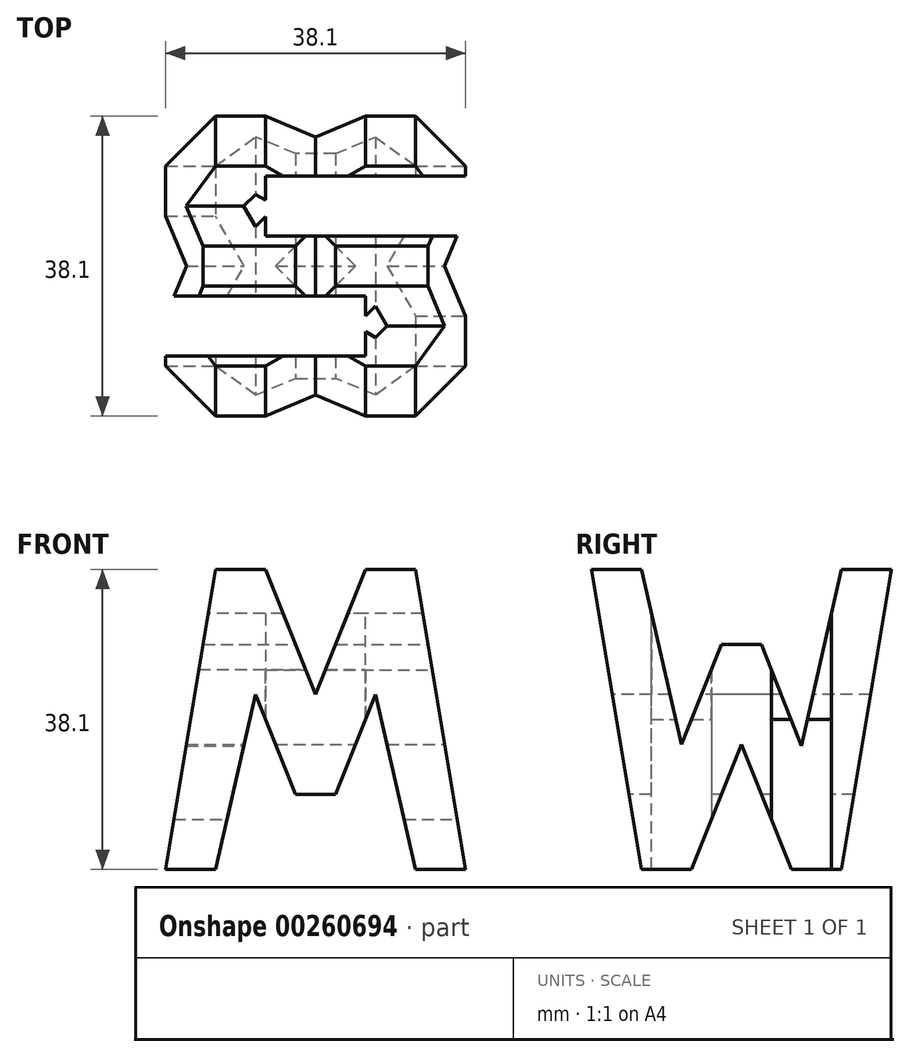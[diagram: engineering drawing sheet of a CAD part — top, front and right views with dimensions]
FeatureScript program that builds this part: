
annotation { "Feature Type Name" : "Feature", "Feature Type Description" : "" }
export const myFeature = defineFeature(function(context is Context, id is Id, definition is map)
    precondition{}
    {
        {
            var Q0;
            Q0=qCreatedBy(makeId("Front.planeOp"),FACE);
            var sketch = newSketch(context, id + "F0", { "sketchPlane" : qUnion([Q0])});
            skLineSegment(sketch, "E0", {"start": v(0, 0) * mm, "end": v(0, 38.1) * mm});
            skLineSegment(sketch, "E1", {"start": v(0, 0) * mm, "end": v(38.1, 0) * mm});
            skLineSegment(sketch, "E2", {"start": v(38.1, 0) * mm, "end": v(38.1, 38.1) * mm});
            skLineSegment(sketch, "E3", {"start": v(38.1, 38.1) * mm, "end": v(0, 38.1) * mm});
            skSolve(sketch);
        }
        {
            var Q0;
            Q0 = qSketchRegion(id + "F0", true);
            extrude(context, id + "F1", {"entities" : qUnion([Q0]), "depth" : 38.1 * mm});
        }
        {
            var Q0;
            Q0=qCreatedBy(makeId("Front.planeOp"),FACE);
            cPlane(context, id + "F2", {"entities" : qUnion([Q0]), "cplaneType" : CPlaneType.OFFSET, "offset" : 38.1 * mm, "width" : 152.4 * mm, "height" : 152.4 * mm});
        }
        {
            var Q0;
            Q0=qCreatedBy(makeId("Right.planeOp"),FACE);
            cPlane(context, id + "F3", {"entities" : qUnion([Q0]), "cplaneType" : CPlaneType.OFFSET, "offset" : 38.1 * mm, "width" : 152.4 * mm, "height" : 152.4 * mm});
        }
        {
            var Q0;
            Q0=qCreatedBy(makeId("Top.planeOp"),FACE);
            cPlane(context, id + "F4", {"entities" : qUnion([Q0]), "cplaneType" : CPlaneType.OFFSET, "offset" : 38.1 * mm, "width" : 152.4 * mm, "height" : 152.4 * mm});
        }
        {
            var Q0;
            Q0=qCreatedBy(id+"F3.planeOp",FACE);
            var sketch = newSketch(context, id + "F5", { "sketchPlane" : qUnion([Q0])});
            skLineSegment(sketch, "E4", {"start": v(0, 0) * mm, "end": v(0, 38.1) * mm});
            skLineSegment(sketch, "E5", {"start": v(0, 38.1) * mm, "end": v(-38.1, 38.1) * mm});
            skLineSegment(sketch, "E6", {"start": v(-38.1, 38.1) * mm, "end": v(-38.1, 0) * mm});
            skPoint(sketch, "E7.start.orphan", {"position": v(-19.05, 15.87) * mm});
            skPoint(sketch, "E8.start.orphan", {"position": v(-12.7, 0) * mm});
            skLineSegment(sketch, "E9", {"start": v(-6.35, 38.1) * mm, "end": v(-11.43, 15.67) * mm});
            skLineSegment(sketch, "E10", {"start": v(-11.43, 15.67) * mm, "end": v(-16.5, 28.57) * mm});
            skLineSegment(sketch, "E11", {"start": v(-16.5, 28.57) * mm, "end": v(-21.59, 28.57) * mm});
            skLineSegment(sketch, "E12", {"start": v(-21.59, 28.57) * mm, "end": v(-26.67, 15.87) * mm});
            skLineSegment(sketch, "E13", {"start": v(-26.67, 15.87) * mm, "end": v(-31.75, 38.1) * mm});
            skPoint(sketch, "E14.start.orphan", {"position": v(-31.75, 0) * mm});
            skPoint(sketch, "E15.start.orphan", {"position": v(-6.35, 0) * mm});
            skLineSegment(sketch, "E16", {"start": v(0, 38.1) * mm, "end": v(-6.35, 0) * mm});
            skLineSegment(sketch, "E17", {"start": v(-19.05, 15.87) * mm, "end": v(-25.4, 0) * mm});
            skLineSegment(sketch, "E18", {"start": v(-25.4, 0) * mm, "end": v(-31.75, 0) * mm});
            skLineSegment(sketch, "E19", {"start": v(-31.75, 0) * mm, "end": v(-38.1, 38.1) * mm});
            skLineSegment(sketch, "E20", {"start": v(-12.7, 0) * mm, "end": v(-6.35, 0) * mm});
            skLineSegment(sketch, "E21", {"start": v(-12.7, 0) * mm, "end": v(-19.05, 15.87) * mm});
            skLineSegment(sketch, "E22", {"start": v(-38.1, 0) * mm, "end": v(0, 0) * mm});
            skSolve(sketch);
        }
        {
            var Q0;
            {var subQ0=sQuery(id+"F5.wireOp",EDGE,"E9");Q0=makeQuery(id+"F5.imprint","IMPRINT",FACE,{"disambiguationData":[TD([[makeQuery(id+"F5.imprint","IMPRINT",EDGE,{"derivedFrom":subQ0}),-1.0]])]});}
            var Q1;
            {var subQ0=sQuery(id+"F5.wireOp",EDGE,"E19");Q1=makeQuery(id+"F5.imprint","IMPRINT",FACE,{"disambiguationData":[TD([[makeQuery(id+"F5.imprint","IMPRINT",EDGE,{"derivedFrom":subQ0}),1.0]])]});}
            var Q2;
            {var subQ0=sQuery(id+"F5.wireOp",EDGE,"E17");Q2=makeQuery(id+"F5.imprint","IMPRINT",FACE,{"disambiguationData":[TD([[makeQuery(id+"F5.imprint","IMPRINT",EDGE,{"derivedFrom":subQ0}),1.0]])]});}
            var Q3;
            {var subQ0=sQuery(id+"F5.wireOp",EDGE,"E4");Q3=makeQuery(id+"F5.imprint","IMPRINT",FACE,{"disambiguationData":[TD([[makeQuery(id+"F5.imprint","IMPRINT",EDGE,{"derivedFrom":subQ0}),1.0]])]});}
            extrude(context, id + "F6", {"entities" : qUnion([Q0, Q1, Q2, Q3]), "operationType" : NewBodyOperationType.REMOVE, "oppositeDirection" : true, "depth" : 38.1 * mm});
        }
        {
            var Q0;
            Q0=qCreatedBy(id+"F2.planeOp",FACE);
            var sketch = newSketch(context, id + "F7", { "sketchPlane" : qUnion([Q0])});
            skLineSegment(sketch, "E23", {"start": v(0, 0) * mm, "end": v(38.1, 0) * mm});
            skLineSegment(sketch, "E24", {"start": v(38.1, 0) * mm, "end": v(38.1, 38.1) * mm});
            skLineSegment(sketch, "E25", {"start": v(38.1, 38.1) * mm, "end": v(0, 38.1) * mm});
            skLineSegment(sketch, "E26", {"start": v(0, 38.1) * mm, "end": v(0, 0) * mm});
            skLineSegment(sketch, "E27", {"start": v(0, 0) * mm, "end": v(6.35, 38.1) * mm});
            skLineSegment(sketch, "E28", {"start": v(12.7, 38.1) * mm, "end": v(19.05, 22.22) * mm});
            skLineSegment(sketch, "E29", {"start": v(19.05, 22.22) * mm, "end": v(25.4, 38.1) * mm});
            skLineSegment(sketch, "E30", {"start": v(38.1, 0) * mm, "end": v(31.75, 38.1) * mm});
            skLineSegment(sketch, "E31", {"start": v(6.35, 0) * mm, "end": v(11.43, 22.23) * mm});
            skLineSegment(sketch, "E32", {"start": v(21.59, 9.52) * mm, "end": v(26.67, 22.22) * mm});
            skLineSegment(sketch, "E33", {"start": v(26.67, 22.22) * mm, "end": v(31.75, 0) * mm});
            skLineSegment(sketch, "E34", {"start": v(21.59, 9.52) * mm, "end": v(16.51, 9.52) * mm});
            skLineSegment(sketch, "E35", {"start": v(16.51, 9.52) * mm, "end": v(11.43, 22.22) * mm});
            skSolve(sketch);
        }
        {
            var Q0;
            {var subQ0=sQuery(id+"F7.wireOp",EDGE,"E26");Q0=makeQuery(id+"F7.imprint","IMPRINT",FACE,{"disambiguationData":[TD([[makeQuery(id+"F7.imprint","IMPRINT",EDGE,{"derivedFrom":subQ0}),1.0]])]});}
            var Q1;
            {var subQ0=sQuery(id+"F7.wireOp",EDGE,"E24");Q1=makeQuery(id+"F7.imprint","IMPRINT",FACE,{"disambiguationData":[TD([[makeQuery(id+"F7.imprint","IMPRINT",EDGE,{"derivedFrom":subQ0}),1.0]])]});}
            var Q2;
            {var subQ0=sQuery(id+"F7.wireOp",EDGE,"E31");Q2=makeQuery(id+"F7.imprint","IMPRINT",FACE,{"disambiguationData":[TD([[makeQuery(id+"F7.imprint","IMPRINT",EDGE,{"derivedFrom":subQ0}),-1.0]])]});}
            var Q3;
            {var subQ0=sQuery(id+"F7.wireOp",EDGE,"E28");Q3=makeQuery(id+"F7.imprint","IMPRINT",FACE,{"disambiguationData":[TD([[makeQuery(id+"F7.imprint","IMPRINT",EDGE,{"derivedFrom":subQ0}),1.0]])]});}
            extrude(context, id + "F8", {"entities" : qUnion([Q0, Q1, Q2, Q3]), "operationType" : NewBodyOperationType.REMOVE, "oppositeDirection" : true, "depth" : 38.1 * mm});
        }
        {
            var Q0;
            Q0=qCreatedBy(id+"F4.planeOp",FACE);
            var sketch = newSketch(context, id + "F9", { "sketchPlane" : qUnion([Q0])});
            skLineSegment(sketch, "E36", {"start": v(0, 0) * mm, "end": v(38.1, 0) * mm});
            skLineSegment(sketch, "E37", {"start": v(38.1, 0) * mm, "end": v(38.1, -38.1) * mm});
            skLineSegment(sketch, "E38", {"start": v(38.1, -38.1) * mm, "end": v(0, -38.1) * mm});
            skLineSegment(sketch, "E39", {"start": v(0, -38.1) * mm, "end": v(0, 0) * mm});
            skLineSegment(sketch, "E40", {"start": v(38.1, -7.62) * mm, "end": v(12.7, -7.62) * mm});
            skLineSegment(sketch, "E41", {"start": v(12.7, -7.62) * mm, "end": v(12.7, -15.24) * mm});
            skLineSegment(sketch, "E42", {"start": v(12.7, -15.24) * mm, "end": v(38.1, -15.24) * mm});
            skLineSegment(sketch, "E43", {"start": v(0, -22.86) * mm, "end": v(25.4, -22.86) * mm});
            skLineSegment(sketch, "E44", {"start": v(25.4, -22.86) * mm, "end": v(25.4, -30.48) * mm});
            skLineSegment(sketch, "E45", {"start": v(25.4, -30.48) * mm, "end": v(0, -30.48) * mm});
            skSolve(sketch);
        }
        {
            var Q0;
            {var subQ0=sQuery(id+"F9.wireOp",EDGE,"E40");Q0=makeQuery(id+"F9.imprint","IMPRINT",FACE,{"disambiguationData":[TD([[makeQuery(id+"F9.imprint","IMPRINT",EDGE,{"derivedFrom":subQ0}),1.0]])]});}
            var Q1;
            {var subQ0=sQuery(id+"F9.wireOp",EDGE,"E43");Q1=makeQuery(id+"F9.imprint","IMPRINT",FACE,{"disambiguationData":[TD([[makeQuery(id+"F9.imprint","IMPRINT",EDGE,{"derivedFrom":subQ0}),-1.0]])]});}
            extrude(context, id + "F10", {"entities" : qUnion([Q0, Q1]), "operationType" : NewBodyOperationType.REMOVE, "oppositeDirection" : true, "depth" : 38.1 * mm, "offsetDistance" : 25.4 * mm});
        }
    });
